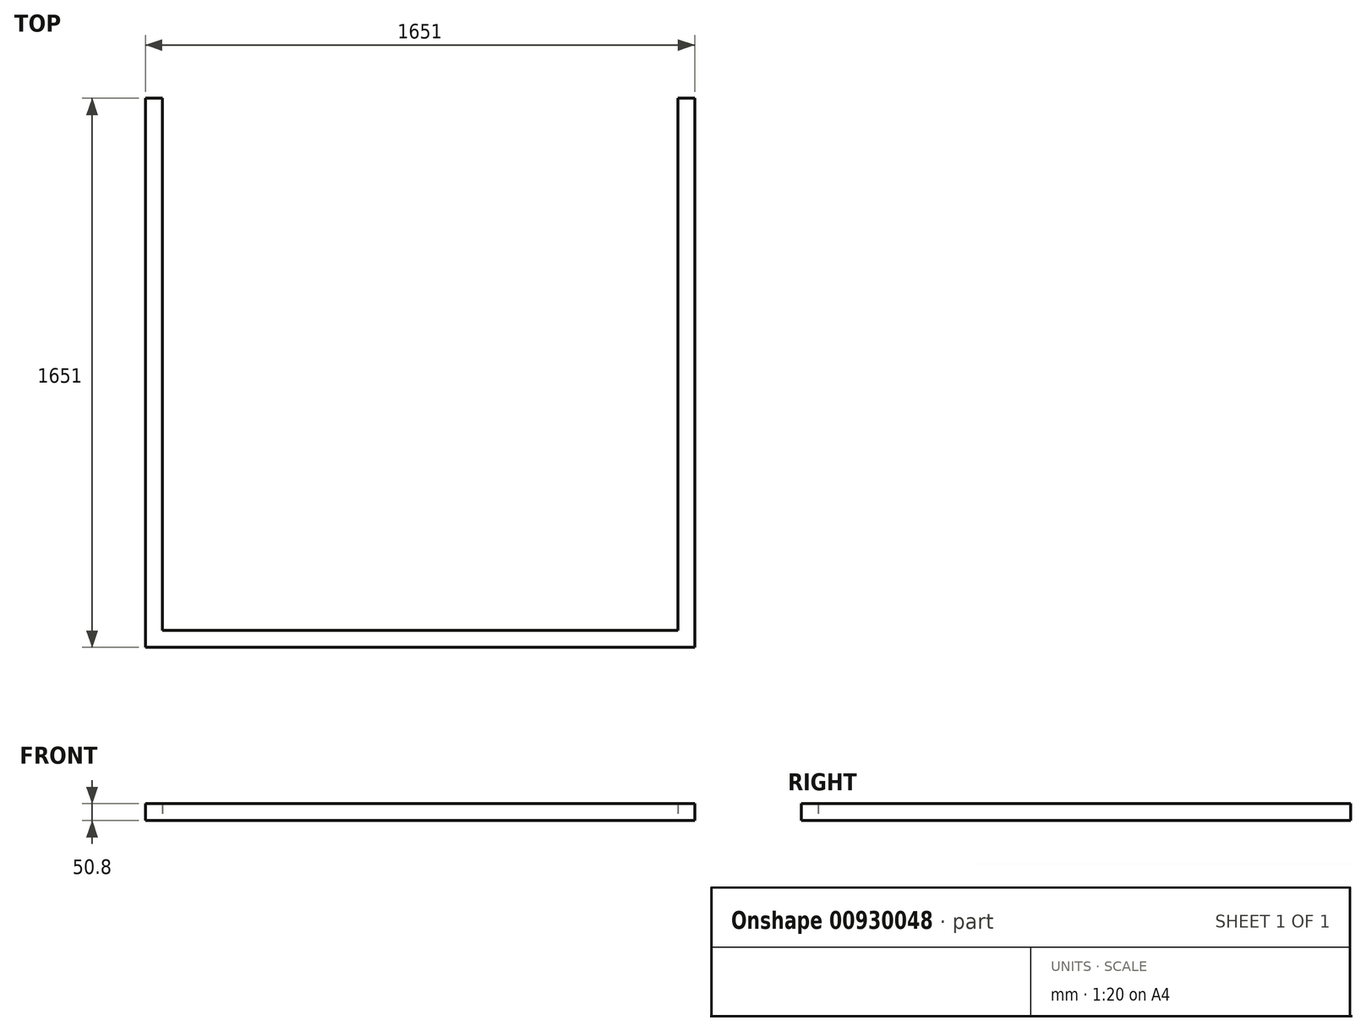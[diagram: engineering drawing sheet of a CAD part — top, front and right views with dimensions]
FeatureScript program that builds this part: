
annotation { "Feature Type Name" : "Feature", "Feature Type Description" : "" }
export const myFeature = defineFeature(function(context is Context, id is Id, definition is map)
    precondition{}
    {
        {
            var Q0;
            Q0=qCreatedBy(makeId("Top.planeOp"),FACE);
            var sketch = newSketch(context, id + "F0", { "sketchPlane" : qUnion([Q0])});
            skLineSegment(sketch, "E0.bottom", {"start": v(-825.5, 825.5) * mm, "end": v(-774.7, 825.5) * mm});
            skLineSegment(sketch, "E0.top", {"start": v(-825.5, -825.5) * mm, "end": v(825.5, -825.5) * mm});
            skLineSegment(sketch, "E0.left", {"start": v(-825.5, 825.5) * mm, "end": v(-825.5, -825.5) * mm});
            skLineSegment(sketch, "E0.right", {"start": v(825.5, 825.5) * mm, "end": v(825.5, -825.5) * mm});
            skLineSegment(sketch, "E1.top", {"start": v(-774.7, -774.7) * mm, "end": v(774.7, -774.7) * mm});
            skLineSegment(sketch, "E1.left", {"start": v(-774.7, 825.5) * mm, "end": v(-774.7, -774.7) * mm});
            skLineSegment(sketch, "E1.right", {"start": v(774.7, 825.5) * mm, "end": v(774.7, -774.7) * mm});
            skLineSegment(sketch, "E2.trimOffspring", {"start": v(774.7, 825.5) * mm, "end": v(825.5, 825.5) * mm});
            skSolve(sketch);
        }
        {
            var Q0;
            Q0=makeQuery(id+"F0.imprint","IMPRINT",FACE,{"disambiguationData":[TD([[makeQuery(id+"F0.imprint","IMPRINT",EDGE,{"derivedFrom":sQuery(id+"F0.wireOp",EDGE,"E0.bottom")}),-1.0]])]});
            extrude(context, id + "F1", {"entities" : qUnion([Q0]), "depth" : 50.8 * mm, "offsetDistance" : 25.4 * mm});
        }
    });
